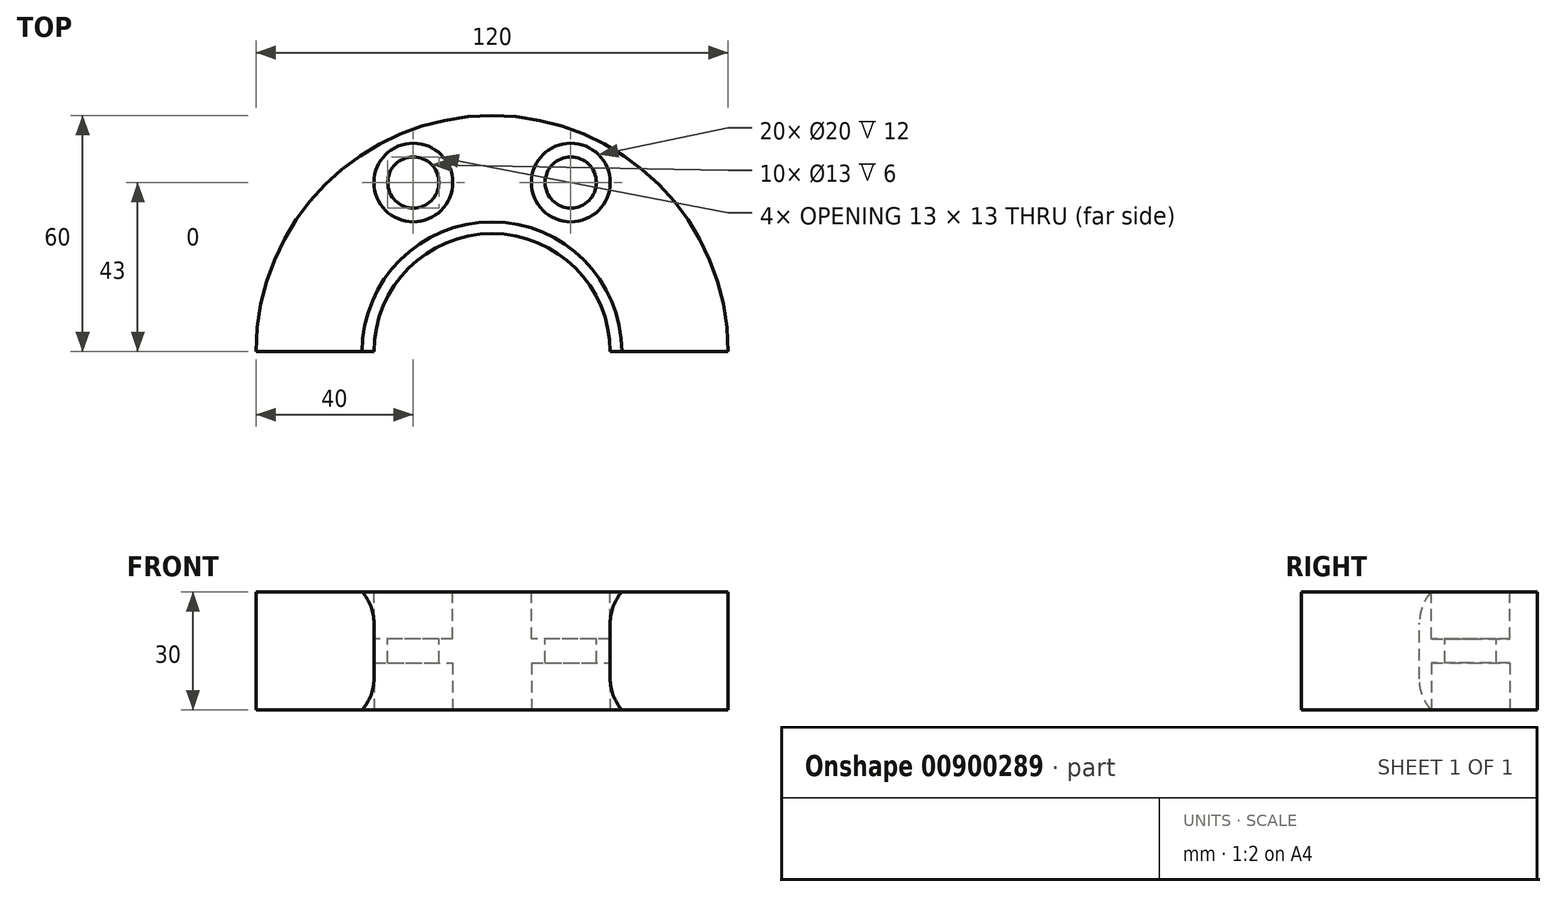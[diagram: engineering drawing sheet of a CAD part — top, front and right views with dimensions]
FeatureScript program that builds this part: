
annotation { "Feature Type Name" : "Feature", "Feature Type Description" : "" }
export const myFeature = defineFeature(function(context is Context, id is Id, definition is map)
    precondition{}
    {
        {
            var Q0;
            Q0=qCreatedBy(makeId("Top.planeOp"),FACE);
            var sketch = newSketch(context, id + "F0", { "sketchPlane" : qUnion([Q0])});
            skArc(sketch, "E0", {"start": v(60, 0) * mm, "mid": v(0, 60) * mm, "end": v(-60, 0) * mm});
            skArc(sketch, "E1", {"start": v(30, 0) * mm, "mid": v(0, 30) * mm, "end": v(-30, 0) * mm});
            skLineSegment(sketch, "E2", {"start": v(-60, 0) * mm, "end": v(-30, 0) * mm});
            skLineSegment(sketch, "E3.trimOffspring", {"start": v(30, 0) * mm, "end": v(60, 0) * mm});
            skSolve(sketch);
        }
        {
            var Q0;
            Q0 = qSketchRegion(id + "F0", true);
            extrude(context, id + "F1", {"entities" : qUnion([Q0]), "oppositeDirection" : true, "depth" : 30 * mm, "offsetDistance" : 25 * mm});
        }
        {
            var Q0;
            Q0=makeQuery(id+"F1.opExtrude","CAP_FACE",FACE,{"disambiguationData":[OSD([sQuery(id+"F0.wireOp",EDGE,"E0"),sQuery(id+"F0.wireOp",EDGE,"E1"),sQuery(id+"F0.wireOp",EDGE,"E2"),sQuery(id+"F0.wireOp",EDGE,"E3.trimOffspring")])],"isStart":true});
            var sketch = newSketch(context, id + "F2", { "sketchPlane" : qUnion([Q0])});
            skCircle(sketch, "E4", {"center": v(0, 0) * mm, "radius": 47.42 * mm, "construction": true});
            skCircle(sketch, "E5", {"center": v(20, 43) * mm, "radius": 6.5 * mm});
            skCircle(sketch, "E6.MirrorC", {"center": v(-20, 43) * mm, "radius": 6.5 * mm});
            skSolve(sketch);
        }
        {
            var Q0;
            Q0 = qSketchRegion(id + "F2", true);
            extrude(context, id + "F3", {"entities" : qUnion([Q0]), "operationType" : NewBodyOperationType.REMOVE, "endBound" : BoundingType.UP_TO_NEXT, "oppositeDirection" : true, "depth" : 25 * mm, "offsetDistance" : 25 * mm});
        }
        {
            var Q0;
            Q0=makeQuery(id+"F1.opExtrude","CAP_FACE",FACE,{"disambiguationData":[OSD([sQuery(id+"F0.wireOp",EDGE,"E0"),sQuery(id+"F0.wireOp",EDGE,"E1"),sQuery(id+"F0.wireOp",EDGE,"E2"),sQuery(id+"F0.wireOp",EDGE,"E3.trimOffspring")])],"isStart":true});
            var sketch = newSketch(context, id + "F4", { "sketchPlane" : qUnion([Q0])});
            skCircle(sketch, "E7", {"center": v(20, 43) * mm, "radius": 10 * mm});
            skCircle(sketch, "E8", {"center": v(-20, 43) * mm, "radius": 10 * mm});
            skSolve(sketch);
        }
        {
            var Q0;
            Q0 = qSketchRegion(id + "F4", true);
            extrude(context, id + "F5", {"entities" : qUnion([Q0]), "operationType" : NewBodyOperationType.REMOVE, "oppositeDirection" : true, "depth" : 12 * mm, "offsetDistance" : 25 * mm});
        }
        {
            var Q0;
            Q0=makeQuery(id+"F1.opExtrude","CAP_FACE",FACE,{"disambiguationData":[OSD([sQuery(id+"F0.wireOp",EDGE,"E0"),sQuery(id+"F0.wireOp",EDGE,"E1"),sQuery(id+"F0.wireOp",EDGE,"E2"),sQuery(id+"F0.wireOp",EDGE,"E3.trimOffspring")])],"isStart":false});
            var sketch = newSketch(context, id + "F6", { "sketchPlane" : qUnion([Q0])});
            skCircle(sketch, "E9", {"center": v(-20, -43) * mm, "radius": 10 * mm});
            skCircle(sketch, "E10", {"center": v(20, -43) * mm, "radius": 10 * mm});
            skSolve(sketch);
        }
        {
            var Q0;
            Q0 = qSketchRegion(id + "F6", true);
            extrude(context, id + "F7", {"entities" : qUnion([Q0]), "operationType" : NewBodyOperationType.REMOVE, "oppositeDirection" : true, "depth" : 12 * mm, "offsetDistance" : 25 * mm});
        }
        {
            var Q0;
            Q0=makeQuery(id+"F1.opExtrude","CAP_EDGE",EDGE,{"disambiguationData":[OSD([sQuery(id+"F0.wireOp",EDGE,"E1")])],"isStart":false});
            var Q1;
            Q1=makeQuery(id+"F1.opExtrude","CAP_EDGE",EDGE,{"disambiguationData":[OSD([sQuery(id+"F0.wireOp",EDGE,"E1")])],"isStart":true});
            chamfer(context, id + "F8", {"entities" : qUnion([Q0, Q1]), "width" : 3 * mm, "tangentPropagation" : true});
        }
        {
            var Q0;
            {var subQ0=sQuery(id+"F0.wireOp",EDGE,"E1");Q0=makeQuery(id+"F8.opChamfer","BLEND_EDGE",EDGE,{"blendedFrom":[makeQuery(id+"F1.opExtrude","CAP_EDGE",EDGE,{"disambiguationData":[OSD([subQ0])],"isStart":false}),makeQuery(id+"F1.opExtrude","SWEPT_FACE",FACE,{"disambiguationData":[OSD([subQ0])]})],"blendedInto":[makeQuery(id+"F1.opExtrude","SWEPT_FACE",FACE,{"disambiguationData":[OSD([subQ0])]})]});}
            var Q1;
            {var subQ0=sQuery(id+"F0.wireOp",EDGE,"E1");Q1=makeQuery(id+"F8.opChamfer","BLEND_EDGE",EDGE,{"blendedFrom":[makeQuery(id+"F1.opExtrude","CAP_EDGE",EDGE,{"disambiguationData":[OSD([subQ0])],"isStart":true}),makeQuery(id+"F1.opExtrude","SWEPT_FACE",FACE,{"disambiguationData":[OSD([subQ0])]})],"blendedInto":[makeQuery(id+"F1.opExtrude","SWEPT_FACE",FACE,{"disambiguationData":[OSD([subQ0])]})]});}
            fillet(context, id + "F9", {"entities" : qUnion([Q0, Q1]), "radius" : 12 * mm, "tangentPropagation" : true, "allowEdgeOverflow" : false});
        }
    });
